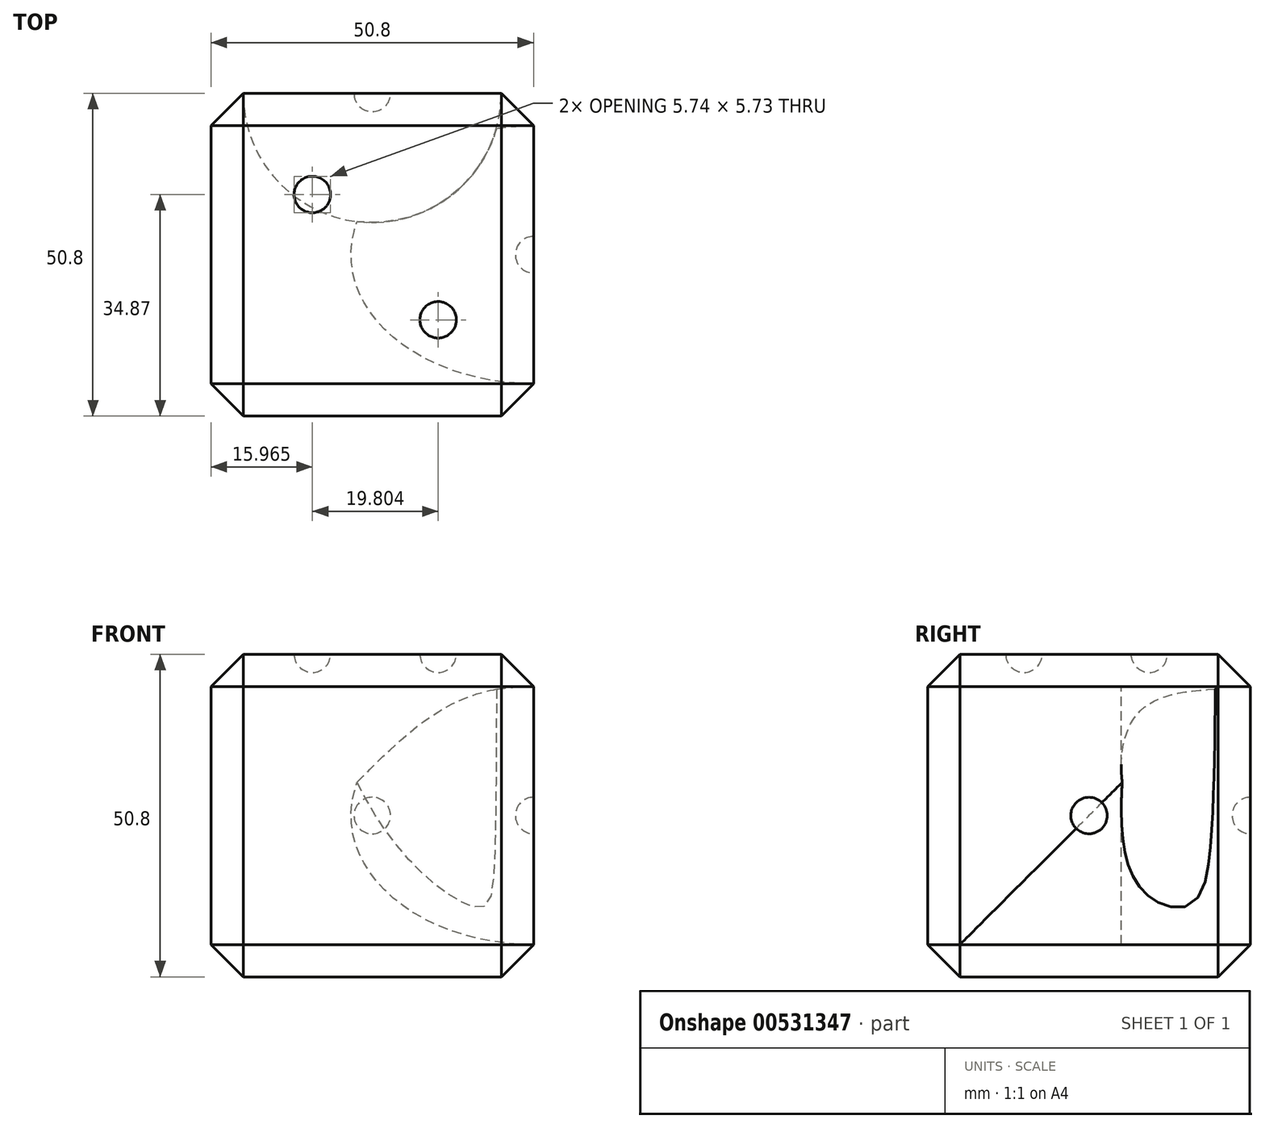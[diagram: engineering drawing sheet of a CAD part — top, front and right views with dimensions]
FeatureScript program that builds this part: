
annotation { "Feature Type Name" : "Feature", "Feature Type Description" : "" }
export const myFeature = defineFeature(function(context is Context, id is Id, definition is map)
    precondition{}
    {
        {
            var Q0;
            Q0=qCreatedBy(makeId("Front.planeOp"),FACE);
            var sketch = newSketch(context, id + "F0", { "sketchPlane" : qUnion([Q0])});
            skLineSegment(sketch, "E0", {"start": v(0, 0) * mm, "end": v(0, 50.8) * mm});
            skLineSegment(sketch, "E1", {"start": v(0, 50.8) * mm, "end": v(50.8, 50.8) * mm});
            skLineSegment(sketch, "E2", {"start": v(50.8, 50.8) * mm, "end": v(50.8, 0) * mm});
            skLineSegment(sketch, "E3", {"start": v(0, 0) * mm, "end": v(50.8, 0) * mm});
            skSolve(sketch);
        }
        {
            var Q0;
            Q0=makeQuery(id+"F0.imprint","IMPRINT",FACE,{"disambiguationData":[TD([[makeQuery(id+"F0.imprint","IMPRINT",EDGE,{"derivedFrom":sQuery(id+"F0.wireOp",EDGE,"E0")}),-1.0]])]});
            extrude(context, id + "F1", {"entities" : qUnion([Q0]), "depth" : 50.8 * mm, "offsetDistance" : 25.4 * mm});
        }
        {
            var Q0;
            Q0=makeQuery(id+"F1.opExtrude","CAP_EDGE",EDGE,{"disambiguationData":[OSD([sQuery(id+"F0.wireOp",EDGE,"E1")])],"isStart":false});
            var Q1;
            Q1=makeQuery(id+"F1.opExtrude","CAP_FACE",FACE,{"disambiguationData":[OSD([sQuery(id+"F0.wireOp",EDGE,"E0"),sQuery(id+"F0.wireOp",EDGE,"E1"),sQuery(id+"F0.wireOp",EDGE,"E2"),sQuery(id+"F0.wireOp",EDGE,"E3")])],"isStart":false});
            var Q2;
            Q2=makeQuery(id+"F1.opExtrude","SWEPT_EDGE",EDGE,{"disambiguationData":[OSD([sQuery(id+"F0.wireOp",EDGE,"E1"),sQuery(id+"F0.wireOp",EDGE,"E2")])]});
            var Q3;
            Q3=makeQuery(id+"F1.opExtrude","CAP_EDGE",EDGE,{"disambiguationData":[OSD([sQuery(id+"F0.wireOp",EDGE,"E1")])],"isStart":true});
            var Q4;
            Q4=makeQuery(id+"F1.opExtrude","SWEPT_FACE",FACE,{"disambiguationData":[OSD([sQuery(id+"F0.wireOp",EDGE,"E1")])]});
            var Q5;
            Q5=makeQuery(id+"F1.opExtrude","CAP_EDGE",EDGE,{"disambiguationData":[OSD([sQuery(id+"F0.wireOp",EDGE,"E0")])],"isStart":true});
            var Q6;
            Q6=makeQuery(id+"F1.opExtrude","CAP_EDGE",EDGE,{"disambiguationData":[OSD([sQuery(id+"F0.wireOp",EDGE,"E3")])],"isStart":true});
            var Q7;
            Q7=makeQuery(id+"F1.opExtrude","CAP_EDGE",EDGE,{"disambiguationData":[OSD([sQuery(id+"F0.wireOp",EDGE,"E2")])],"isStart":true});
            var Q8;
            Q8=makeQuery(id+"F1.opExtrude","SWEPT_EDGE",EDGE,{"disambiguationData":[OSD([sQuery(id+"F0.wireOp",EDGE,"E0"),sQuery(id+"F0.wireOp",EDGE,"E3")])]});
            var Q9;
            Q9=makeQuery(id+"F1.opExtrude","SWEPT_EDGE",EDGE,{"disambiguationData":[OSD([sQuery(id+"F0.wireOp",EDGE,"E2"),sQuery(id+"F0.wireOp",EDGE,"E3")])]});
            chamfer(context, id + "F2", {"entities" : qUnion([Q0, Q1, Q2, Q3, Q4, Q5, Q6, Q7, Q8, Q9]), "width" : 5.08 * mm, "tangentPropagation" : true});
        }
        {
            var Q0;
            Q0=makeQuery(id+"F1.opExtrude","CAP_FACE",FACE,{"disambiguationData":[OSD([sQuery(id+"F0.wireOp",EDGE,"E0"),sQuery(id+"F0.wireOp",EDGE,"E1"),sQuery(id+"F0.wireOp",EDGE,"E2"),sQuery(id+"F0.wireOp",EDGE,"E3")])],"isStart":true});
            var sketch = newSketch(context, id + "F3", { "sketchPlane" : qUnion([Q0])});
            skLineSegment(sketch, "E4", {"start": v(-25.4, 5.08) * mm, "end": v(-25.4, 45.72) * mm});
            skCircle(sketch, "E5", {"center": v(-25.4, 25.4) * mm, "radius": 2.88 * mm});
            skSolve(sketch);
        }
        {
            var Q0;
            {var subQ0=sQuery(id+"F3.wireOp",EDGE,"E5");var subQ1=sQuery(id+"F3.wireOp",EDGE,"E4");var subQ2=makeQuery(id+"F3.imprint","INTERSECT",VERTEX,{"disambiguationData":[OD(0.0)],"derivedFrom":[subQ1,subQ0]});Q0=makeQuery(id+"F3.imprint","IMPRINT",FACE,{"disambiguationData":[TD([[makeQuery(id+"F3.imprint","IMPRINT",EDGE,{"disambiguationData":[TD([[subQ2,-1.0]])],"derivedFrom":subQ1}),-1.0]])]});}
            var Q1;
            Q1=sQuery(id+"F3.wireOp",EDGE,"E4");
            revolve(context, id + "F4", {"operationType" : NewBodyOperationType.REMOVE, "entities" : qUnion([Q0]), "axis" : qUnion([Q1]), "revolveType" : RevolveType.FULL, "oppositeDirection" : true});
        }
        {
            var Q0;
            Q0=makeQuery(id+"F1.opExtrude","SWEPT_FACE",FACE,{"disambiguationData":[OSD([sQuery(id+"F0.wireOp",EDGE,"E1")])]});
            var sketch = newSketch(context, id + "F5", { "sketchPlane" : qUnion([Q0])});
            skLineSegment(sketch, "E6", {"start": v(45.72, -45.72) * mm, "end": v(45.4, -45.25) * mm});
            skCircle(sketch, "E7", {"center": v(15.97, -15.92) * mm, "radius": 2.87 * mm});
            skCircle(sketch, "E8", {"center": v(35.77, -35.65) * mm, "radius": 2.87 * mm});
            skLineSegment(sketch, "E9", {"start": v(45.4, -45.25) * mm, "end": v(5.08, -5.08) * mm});
            skSolve(sketch);
        }
        {
            var Q0;
            {var subQ0=sQuery(id+"F5.wireOp",EDGE,"E9");var subQ1=sQuery(id+"F5.wireOp",EDGE,"E8");var subQ2=makeQuery(id+"F5.imprint","INTERSECT",VERTEX,{"disambiguationData":[OD(0.0)],"derivedFrom":[subQ1,subQ0]});Q0=makeQuery(id+"F5.imprint","IMPRINT",FACE,{"disambiguationData":[TD([[makeQuery(id+"F5.imprint","IMPRINT",EDGE,{"disambiguationData":[TD([[subQ2,1.0]])],"derivedFrom":subQ1}),1.0]])]});}
            var Q1;
            {var subQ0=sQuery(id+"F5.wireOp",EDGE,"E9");var subQ1=sQuery(id+"F5.wireOp",EDGE,"E7");var subQ2=makeQuery(id+"F5.imprint","INTERSECT",VERTEX,{"disambiguationData":[OD(0.0)],"derivedFrom":[subQ1,subQ0]});Q1=makeQuery(id+"F5.imprint","IMPRINT",FACE,{"disambiguationData":[TD([[makeQuery(id+"F5.imprint","IMPRINT",EDGE,{"disambiguationData":[TD([[subQ2,1.0]])],"derivedFrom":subQ1}),1.0]])]});}
            var Q2;
            Q2=sQuery(id+"F5.wireOp",EDGE,"E9");
            revolve(context, id + "F6", {"operationType" : NewBodyOperationType.REMOVE, "entities" : qUnion([Q0, Q1]), "axis" : qUnion([Q2]), "revolveType" : RevolveType.FULL, "oppositeDirection" : true});
        }
        {
            var Q0;
            Q0=makeQuery(id+"F1.opExtrude","SWEPT_FACE",FACE,{"disambiguationData":[OSD([sQuery(id+"F0.wireOp",EDGE,"E2")])]});
            var sketch = newSketch(context, id + "F7", { "sketchPlane" : qUnion([Q0])});
            skLineSegment(sketch, "E10", {"start": v(-45.72, 45.72) * mm, "end": v(-5.08, 5.08) * mm});
            skCircle(sketch, "E11", {"center": v(-35.86, 35.86) * mm, "radius": 2.87 * mm});
            skCircle(sketch, "E12", {"center": v(-25.4, 25.4) * mm, "radius": 2.87 * mm});
            skCircle(sketch, "E13", {"center": v(-13.85, 13.85) * mm, "radius": 2.87 * mm});
            skSolve(sketch);
        }
        {
            var Q0;
            {var subQ0=sQuery(id+"F7.wireOp",EDGE,"E11");var subQ1=sQuery(id+"F7.wireOp",EDGE,"E10");var subQ2=makeQuery(id+"F7.imprint","INTERSECT",VERTEX,{"disambiguationData":[OD(0.0)],"derivedFrom":[subQ1,subQ0]});Q0=makeQuery(id+"F7.imprint","IMPRINT",FACE,{"disambiguationData":[TD([[makeQuery(id+"F7.imprint","IMPRINT",EDGE,{"disambiguationData":[TD([[subQ2,-1.0]])],"derivedFrom":subQ1}),1.0]])]});}
            var Q1;
            {var subQ0=sQuery(id+"F7.wireOp",EDGE,"E12");var subQ1=sQuery(id+"F7.wireOp",EDGE,"E10");var subQ2=makeQuery(id+"F7.imprint","INTERSECT",VERTEX,{"disambiguationData":[OD(0.0)],"derivedFrom":[subQ1,subQ0]});Q1=makeQuery(id+"F7.imprint","IMPRINT",FACE,{"disambiguationData":[TD([[makeQuery(id+"F7.imprint","IMPRINT",EDGE,{"disambiguationData":[TD([[subQ2,-1.0]])],"derivedFrom":subQ1}),1.0]])]});}
            var Q2;
            {var subQ0=sQuery(id+"F7.wireOp",EDGE,"E13");var subQ1=sQuery(id+"F7.wireOp",EDGE,"E10");var subQ2=makeQuery(id+"F7.imprint","INTERSECT",VERTEX,{"disambiguationData":[OD(0.0)],"derivedFrom":[subQ1,subQ0]});Q2=makeQuery(id+"F7.imprint","IMPRINT",FACE,{"disambiguationData":[TD([[makeQuery(id+"F7.imprint","IMPRINT",EDGE,{"disambiguationData":[TD([[subQ2,-1.0]])],"derivedFrom":subQ1}),1.0]])]});}
            var Q3;
            Q3=sQuery(id+"F7.wireOp",EDGE,"E10");
            revolve(context, id + "F8", {"operationType" : NewBodyOperationType.REMOVE, "entities" : qUnion([Q0, Q1, Q2]), "axis" : qUnion([Q3]), "revolveType" : RevolveType.FULL, "oppositeDirection" : true});
        }
    });
